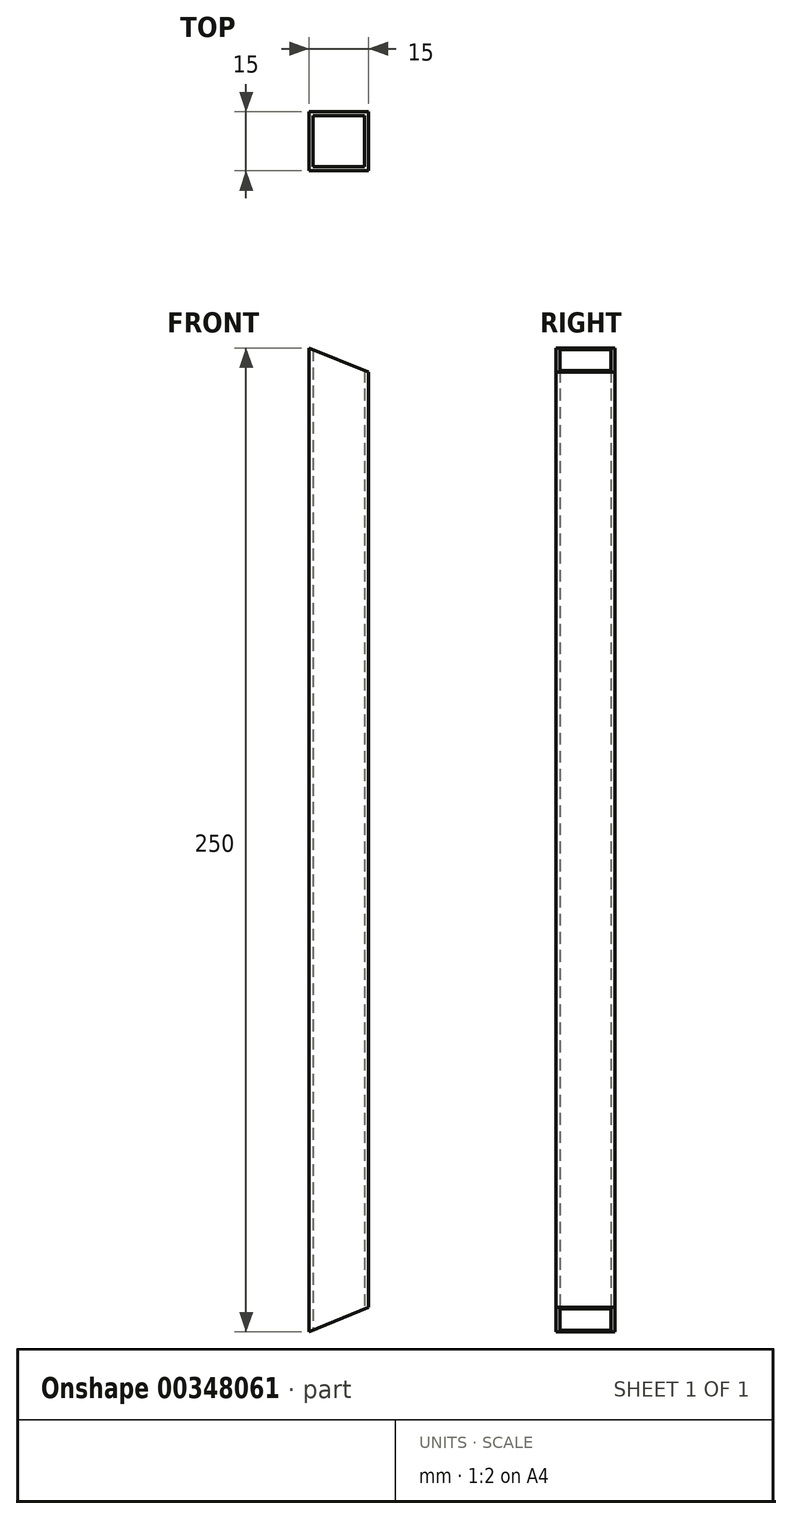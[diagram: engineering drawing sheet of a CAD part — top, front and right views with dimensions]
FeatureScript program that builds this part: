
annotation { "Feature Type Name" : "Feature", "Feature Type Description" : "" }
export const myFeature = defineFeature(function(context is Context, id is Id, definition is map)
    precondition{}
    {
        {
            assignVariable(context, id + "F0", {"name" : "BarLength", "anyValue" : 250});
        }
        {
            var Q0;
            Q0=qCreatedBy(makeId("Top.planeOp"),FACE);
            var sketch = newSketch(context, id + "F1", { "sketchPlane" : qUnion([Q0])});
            skLineSegment(sketch, "E0.bottom", {"start": v(-7.5, 7.5) * mm, "end": v(7.5, 7.5) * mm});
            skLineSegment(sketch, "E0.top", {"start": v(-7.5, -7.5) * mm, "end": v(7.5, -7.5) * mm});
            skLineSegment(sketch, "E0.left", {"start": v(-7.5, 7.5) * mm, "end": v(-7.5, -7.5) * mm});
            skLineSegment(sketch, "E0.right", {"start": v(7.5, 7.5) * mm, "end": v(7.5, -7.5) * mm});
            skPoint(sketch, "E0.middle", {"position": v(0, 0) * mm});
            skLineSegment(sketch, "E1.bottom", {"start": v(-6.5, 6.5) * mm, "end": v(6.5, 6.5) * mm});
            skLineSegment(sketch, "E1.top", {"start": v(-6.5, -6.5) * mm, "end": v(6.5, -6.5) * mm});
            skLineSegment(sketch, "E1.left", {"start": v(-6.5, 6.5) * mm, "end": v(-6.5, -6.5) * mm});
            skLineSegment(sketch, "E1.right", {"start": v(6.5, 6.5) * mm, "end": v(6.5, -6.5) * mm});
            skSolve(sketch);
        }
        {
            var Q0;
            Q0=makeQuery(id+"F1.imprint","IMPRINT",FACE,{"disambiguationData":[TD([[makeQuery(id+"F1.imprint","IMPRINT",EDGE,{"derivedFrom":sQuery(id+"F1.wireOp",EDGE,"E0.bottom")}),-1.0]])]});
            extrude(context, id + "F2", {"entities" : qUnion([Q0]), "depth" : (getVariable(context, 'BarLength')) * mm});
        }
        {
            var Q0;
            Q0=makeQuery(id+"F2.opExtrude","SWEPT_FACE",FACE,{"disambiguationData":[OSD([sQuery(id+"F1.wireOp",EDGE,"E0.top")])]});
            var sketch = newSketch(context, id + "F3", { "sketchPlane" : qUnion([Q0])});
            skLineSegment(sketch, "E2", {"start": v(-7.5, 250) * mm, "end": v(7.5, 250) * mm});
            skLineSegment(sketch, "E3", {"start": v(7.5, 250) * mm, "end": v(7.5, 243.79) * mm});
            skLineSegment(sketch, "E4", {"start": v(7.5, 243.79) * mm, "end": v(-7.5, 250) * mm});
            skLineSegment(sketch, "E5", {"start": v(-7.5, 0) * mm, "end": v(7.5, 0) * mm});
            skLineSegment(sketch, "E6", {"start": v(7.5, 0) * mm, "end": v(7.5, 6.21) * mm});
            skLineSegment(sketch, "E7", {"start": v(7.5, 6.21) * mm, "end": v(-7.5, 0) * mm});
            skSolve(sketch);
        }
        {
            var Q0;
            Q0=makeQuery(id+"F3.imprint","IMPRINT",FACE,{"disambiguationData":[TD([[makeQuery(id+"F3.imprint","IMPRINT",EDGE,{"derivedFrom":sQuery(id+"F3.wireOp",EDGE,"E5")}),1.0]])]});
            var Q1;
            Q1=makeQuery(id+"F3.imprint","IMPRINT",FACE,{"disambiguationData":[TD([[makeQuery(id+"F3.imprint","IMPRINT",EDGE,{"derivedFrom":sQuery(id+"F3.wireOp",EDGE,"E2")}),-1.0]])]});
            extrude(context, id + "F4", {"entities" : qUnion([Q0, Q1]), "operationType" : NewBodyOperationType.REMOVE, "oppositeDirection" : true, "depth" : 25 * mm});
        }
    });
